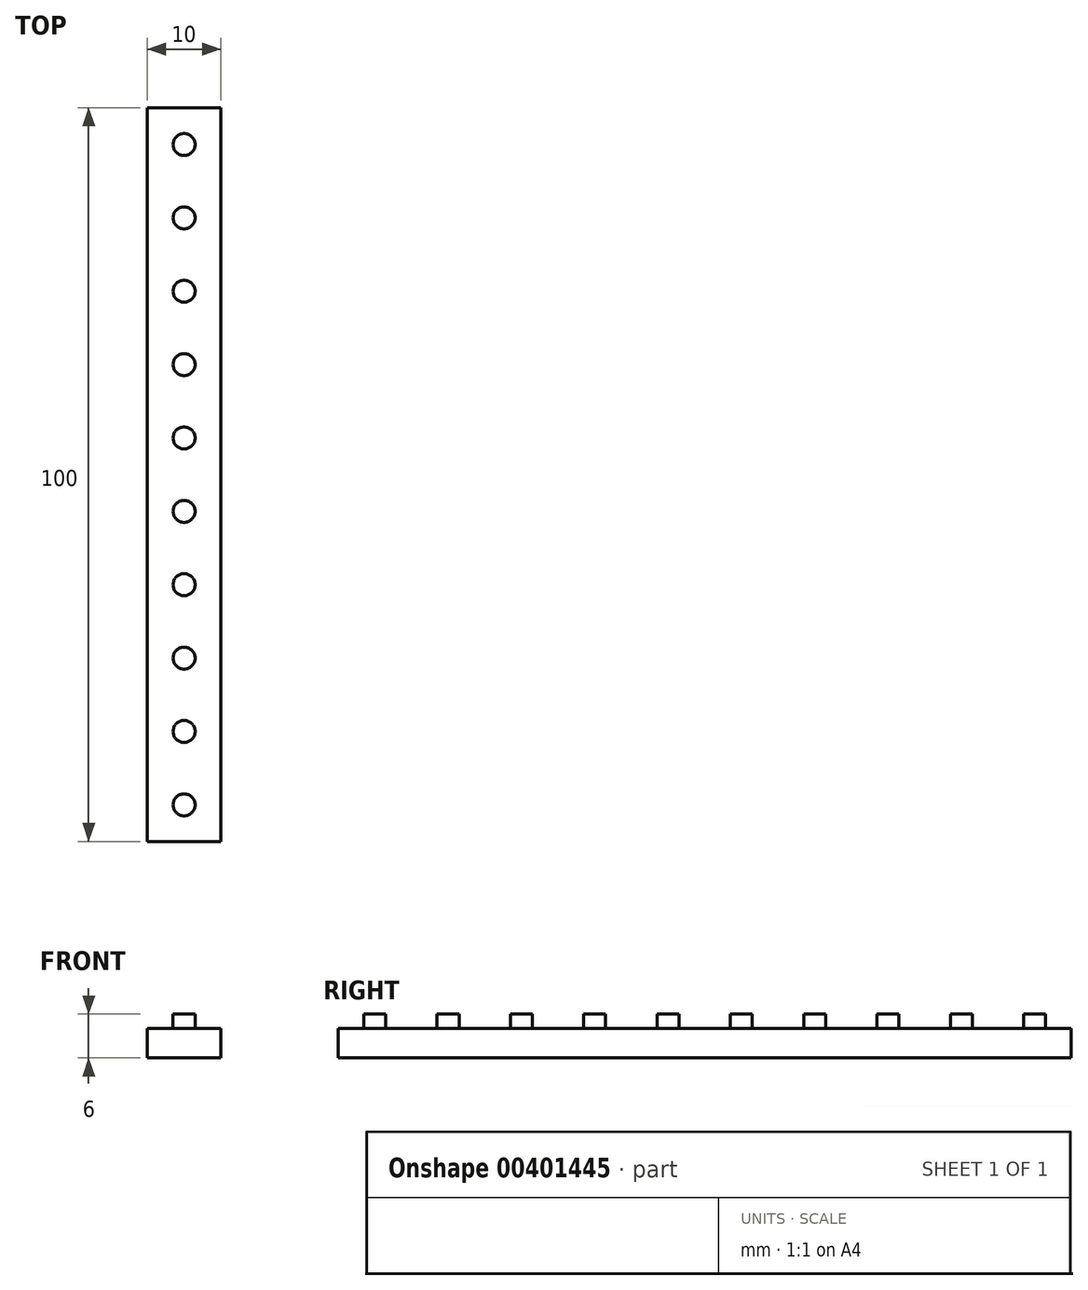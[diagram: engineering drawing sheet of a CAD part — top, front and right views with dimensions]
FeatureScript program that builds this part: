
annotation { "Feature Type Name" : "Feature", "Feature Type Description" : "" }
export const myFeature = defineFeature(function(context is Context, id is Id, definition is map)
    precondition{}
    {
        {
            var Q0;
            Q0=qCreatedBy(makeId("Top.planeOp"),FACE);
            var sketch = newSketch(context, id + "F0", { "sketchPlane" : qUnion([Q0])});
            skLineSegment(sketch, "E0.bottom", {"start": v(-19.89, 67.2) * mm, "end": v(-9.89, 67.2) * mm});
            skLineSegment(sketch, "E0.top", {"start": v(-19.89, -32.8) * mm, "end": v(-9.89, -32.8) * mm});
            skLineSegment(sketch, "E0.left", {"start": v(-19.89, 67.2) * mm, "end": v(-19.89, -32.8) * mm});
            skLineSegment(sketch, "E0.right", {"start": v(-9.89, 67.2) * mm, "end": v(-9.89, -32.8) * mm});
            skLineSegment(sketch, "E1", {"start": v(-14.89, 71.86) * mm, "end": v(-14.89, -38.14) * mm, "construction": true});
            skCircle(sketch, "E2", {"center": v(-14.89, 62.2) * mm, "radius": 1.5 * mm});
            skCircle(sketch, "E3", {"center": v(-14.89, 52.2) * mm, "radius": 1.5 * mm});
            skCircle(sketch, "E4", {"center": v(-14.89, 42.2) * mm, "radius": 1.5 * mm});
            skCircle(sketch, "E5", {"center": v(-14.89, 32.2) * mm, "radius": 1.5 * mm});
            skCircle(sketch, "E6", {"center": v(-14.89, 22.2) * mm, "radius": 1.5 * mm});
            skCircle(sketch, "E7", {"center": v(-14.89, 12.2) * mm, "radius": 1.5 * mm});
            skCircle(sketch, "E8", {"center": v(-14.89, 2.2) * mm, "radius": 1.5 * mm});
            skCircle(sketch, "E9", {"center": v(-14.89, -7.8) * mm, "radius": 1.5 * mm});
            skCircle(sketch, "E10", {"center": v(-14.89, -17.8) * mm, "radius": 1.5 * mm});
            skCircle(sketch, "E11", {"center": v(-14.89, -27.8) * mm, "radius": 1.5 * mm});
            skSolve(sketch);
        }
        {
            var Q0;
            Q0=makeQuery(id+"F0.imprint","IMPRINT",FACE,{"disambiguationData":[TD([[makeQuery(id+"F0.imprint","IMPRINT",EDGE,{"derivedFrom":sQuery(id+"F0.wireOp",EDGE,"E2")}),1.0]])]});
            var Q1;
            Q1=makeQuery(id+"F0.imprint","IMPRINT",FACE,{"disambiguationData":[TD([[makeQuery(id+"F0.imprint","IMPRINT",EDGE,{"derivedFrom":sQuery(id+"F0.wireOp",EDGE,"E3")}),1.0]])]});
            var Q2;
            Q2=makeQuery(id+"F0.imprint","IMPRINT",FACE,{"disambiguationData":[TD([[makeQuery(id+"F0.imprint","IMPRINT",EDGE,{"derivedFrom":sQuery(id+"F0.wireOp",EDGE,"E10")}),1.0]])]});
            var Q3;
            Q3=makeQuery(id+"F0.imprint","IMPRINT",FACE,{"disambiguationData":[TD([[makeQuery(id+"F0.imprint","IMPRINT",EDGE,{"derivedFrom":sQuery(id+"F0.wireOp",EDGE,"E11")}),1.0]])]});
            var Q4;
            Q4=makeQuery(id+"F0.imprint","IMPRINT",FACE,{"disambiguationData":[TD([[makeQuery(id+"F0.imprint","IMPRINT",EDGE,{"derivedFrom":sQuery(id+"F0.wireOp",EDGE,"E4")}),1.0]])]});
            var Q5;
            Q5=makeQuery(id+"F0.imprint","IMPRINT",FACE,{"disambiguationData":[TD([[makeQuery(id+"F0.imprint","IMPRINT",EDGE,{"derivedFrom":sQuery(id+"F0.wireOp",EDGE,"E7")}),1.0]])]});
            var Q6;
            Q6=makeQuery(id+"F0.imprint","IMPRINT",FACE,{"disambiguationData":[TD([[makeQuery(id+"F0.imprint","IMPRINT",EDGE,{"derivedFrom":sQuery(id+"F0.wireOp",EDGE,"E9")}),1.0]])]});
            var Q7;
            Q7=makeQuery(id+"F0.imprint","IMPRINT",FACE,{"disambiguationData":[TD([[makeQuery(id+"F0.imprint","IMPRINT",EDGE,{"derivedFrom":sQuery(id+"F0.wireOp",EDGE,"E5")}),1.0]])]});
            var Q8;
            Q8=makeQuery(id+"F0.imprint","IMPRINT",FACE,{"disambiguationData":[TD([[makeQuery(id+"F0.imprint","IMPRINT",EDGE,{"derivedFrom":sQuery(id+"F0.wireOp",EDGE,"E6")}),1.0]])]});
            var Q9;
            Q9=makeQuery(id+"F0.imprint","IMPRINT",FACE,{"disambiguationData":[TD([[makeQuery(id+"F0.imprint","IMPRINT",EDGE,{"derivedFrom":sQuery(id+"F0.wireOp",EDGE,"E8")}),1.0]])]});
            extrude(context, id + "F1", {"entities" : qUnion([Q0, Q1, Q2, Q3, Q4, Q5, Q6, Q7, Q8, Q9]), "depth" : 6 * mm});
        }
        {
            var Q0;
            Q0=makeQuery(id+"F0.imprint","IMPRINT",FACE,{"disambiguationData":[TD([[makeQuery(id+"F0.imprint","IMPRINT",EDGE,{"derivedFrom":sQuery(id+"F0.wireOp",EDGE,"E0.bottom")}),-1.0]])]});
            extrude(context, id + "F2", {"entities" : qUnion([Q0]), "operationType" : NewBodyOperationType.ADD, "depth" : 4 * mm});
        }
    });
